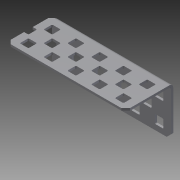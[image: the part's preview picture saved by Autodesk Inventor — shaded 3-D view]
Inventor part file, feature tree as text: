
AUTODESK INVENTOR PART (.ipt)
format: ipt  version: 2014 SP1 (Build 180222100, 222)  size: 850,944 bytes
history: native  units: in
note: dims shown in document units (in); Inventor stores cm internally (conversion verified against a paired STEP export)
features: other x1, imported_body x1, extrude x1, sketch x1
ambient origin geometry x8: Origin, YZ Plane, XZ Plane, XY Plane, X Axis, Y Axis, Z Axis, Center Point
bodies: Body1 (feature_tree)
feature tree (4):
  parser-record x1  (decoder bookkeeping rows leaked as tree rows — omitted from the tree; the rows remain in map.json)
  imported_body  "Base1"
  extrude  "Extrusion1"  Depth=5.0in
  sketch  "Sketch1"  dims[d0=1.0in d1=0.0in d2=5.0in]
